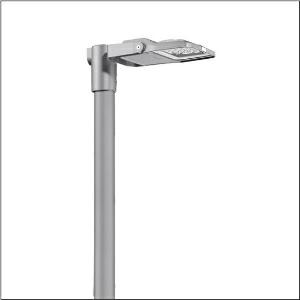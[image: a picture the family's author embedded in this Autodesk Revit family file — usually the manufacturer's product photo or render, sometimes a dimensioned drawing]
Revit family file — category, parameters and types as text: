
# Revit family: floodlight_fl_21_iq_micro___pl33t_5xa7761a4f3a_749b
name_source: partatom
category: Lighting Fixtures
units: mm (PartAtom-declared; Revit-internal decimal feet)

## family parameters
Cut with Voids When Loaded = No
Host = Face
Light Source = No
Part Type = Normal
Room Calculation Point = No
Round Connector Dimension = Use Diameter
Shared = No

## types (1)
- --- (1 x LED, 3050 lm, 23.1 W, 4000K)
    Apparent Load = 23 VA
    CIE Flux Codes = 26 75 99 100 100
    Color Rendering = 70
    Color Temperature = 4000K
    Default Elevation = 1800 mm
    Description = Floodlight FL 21 iQ micro, floodlight, primary light control with lens, of PMMA, primary optical cover: protective disc, of toughened safety glass, transparent, light distribution: PL33T, light emission: direct distribution, installation type: surface-mounted, LED, High Power LED, rated luminous flux: 3.050lm, luminous efficacy: 132lm/W, light colour: 740, colour temperature: 4000K, control: optimised constant luminous flux control (CLO 2.0), Desk-Remote (wireless, voltage-free reading and setting of iQ features in the workshop via application-optimized NFC function/RFID function), Light-Fading, Smart-Wire, Night-Set, Lumen-Switch, Temp-Guard, Auto-Match, with terminal, 6-pole, mains connection: 220..240V, AC, 50/60Hz, start of lifetime: 23W, end of service life: 24W, reduction: 11W, luminaire housing, of diecast aluminium, powder-coated, Siteco® metallic grey (DB 702S), corrosivity category C5 mid according to DIN EN ISO 12944, sealing non-destructively replaceable, please order mast flange separately, mast bracket, of steel, galvanised, powder-coated, Siteco® metallic grey (DB 702S), protection rating (complete): IP66, insulation class (complete): insulation class II (safety insulation), certification: CE, ENEC, VDE, protection symbol: D, impact resistance: IK07, permissible operating ambient temperature: -40..+40°C, permissible operating ambient temperature for outdoor applications: -40..+50°C, standard: DIN EN 12944, LABS conformity tested according to VDMA 24364:2018-05, packaging unit: 1 piece

Light Distribution: PL33T
    Height = 65 mm
    Lamp = 1 x LED
    Lamp Light Flux = 3050 lm
    Lamp Power = 23.1 W
    Lamp count = 1
    Length = 312 mm
    Luminous efficacy = 132 lm/W
    Manufacturer = Siteco
    ModVariant = No
    Model = 5XA7761A4F3A
    Number of Poles = 1
    OnlyDefault = Yes
    Power Factor = 1
    Product Name = Floodlight FL 21 iQ micro | PL33T
    Product group = floodlight | pylon annexe
    ProductGroupID = 6200
    Protection Class = Protection class II
    Protection Degree = IP 66
    RLX_Detail_Level = 1
    RLX_Emergency_Light_Flux = 0 lm
    RLX_Emergency_Type = 0
    RLX_Emergency_Type_DB = No
    RlxData = <blob elided: 101565 chars, md5=5ad2264c>
    Socket = socket
    Standby Power = 0 W
    System Light Flux = 3050 lm
    System Power = 23 W
    Type Comments = factory setting: luminous flux: 100 % | dim-lin: 254 | 455 mA
    Type Image = l_1007121.jpg
    URL = http://relux.com
    VarID = @adj_118451
    Voltage = 0 V
    Weight = 0.00 kg
    Width = 230 mm

## geometry (parser evidence)
native form markers: Blend x4, Sweep x11
no freeform markers — native parametric forms only
